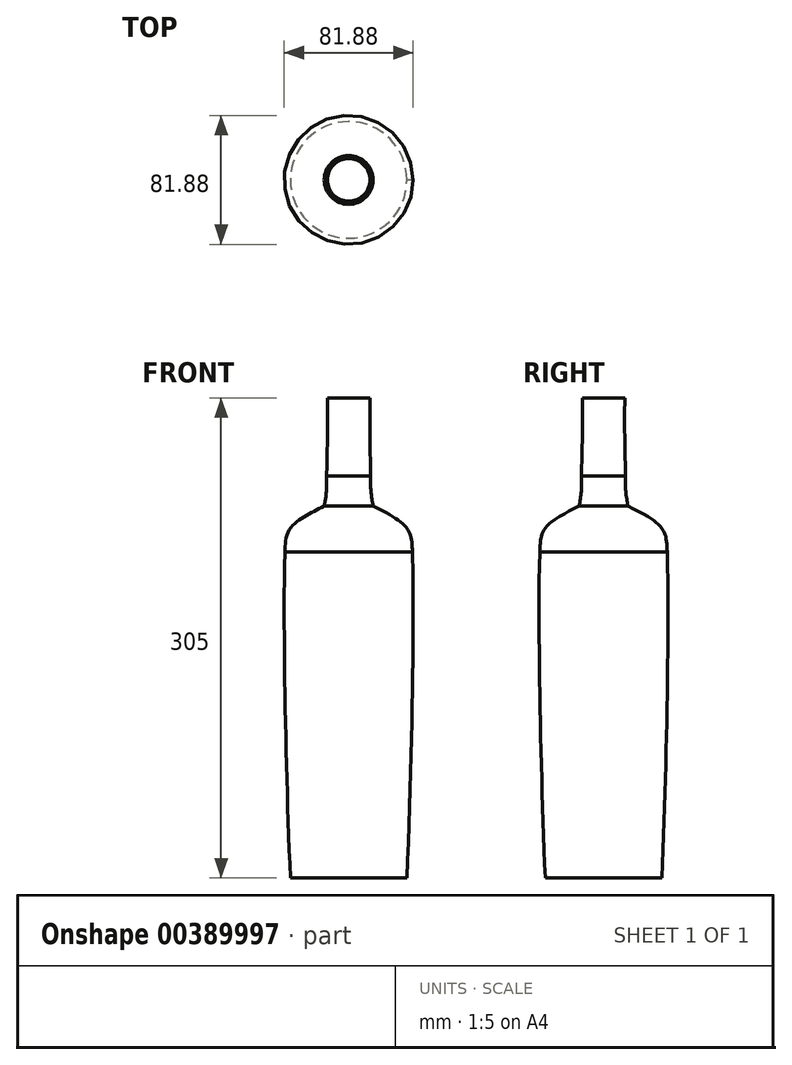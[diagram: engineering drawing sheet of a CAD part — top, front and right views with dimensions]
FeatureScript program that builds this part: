
annotation { "Feature Type Name" : "Feature", "Feature Type Description" : "" }
export const myFeature = defineFeature(function(context is Context, id is Id, definition is map)
    precondition{}
    {
        {
            var Q0;
            Q0=qCreatedBy(makeId("Right.planeOp"),FACE);
            var sketch = newSketch(context, id + "F0", { "sketchPlane" : qUnion([Q0])});
            skLineSegment(sketch, "E0", {"start": v(0, 151.61) * mm, "end": v(0, -153.39) * mm});
            skLineSegment(sketch, "E1", {"start": v(0, -153.39) * mm, "end": v(37, -153.39) * mm});
            skLineSegment(sketch, "E2", {"start": v(0, 53.61) * mm, "end": v(40.5, 53.61) * mm});
            skLineSegment(sketch, "E3", {"start": v(13.5, 151.61) * mm, "end": v(0, 151.61) * mm});
            skLineSegment(sketch, "E4", {"start": v(0, 102.11) * mm, "end": v(13.95, 102.11) * mm});
            skLineSegment(sketch, "E5", {"start": v(0, 82.81) * mm, "end": v(15.55, 82.81) * mm});
            skFitSpline(sketch, "E6", {"points": [v(13.5, 151.61) * mm, v(13.95, 102.11) * mm, v(15.55, 82.81) * mm], "startDerivative": vector(-1.84, -132.19) * mm, "endDerivative": vector(14.94, -74.18) * mm});
            skFitSpline(sketch, "E7", {"points": [v(15.55, 82.81) * mm, v(40.5, 53.61) * mm, v(37, -153.39) * mm], "startDerivative": vector(235.4, -113.87) * mm, "endDerivative": vector(-15.9, -372.84) * mm});
            skSolve(sketch);
        }
        {
            var Q0;
            Q0 = qSketchRegion(id + "F0", true);
            var Q1;
            Q1 = qConstructionFilter(qBodyType(qCreatedBy(id + "F0" ,EDGE), BodyType.WIRE), ConstructionObject.NO);
            var Q2;
            Q2=sQuery(id+"F0.wireOp",EDGE,"E0");
            revolve(context, id + "F1", {"entities" : qUnion([Q0]), "surfaceEntities" : qUnion([Q1]), "axis" : qUnion([Q2]), "revolveType" : RevolveType.FULL});
        }
    });
